FCSTD DOCUMENT  (FreeCAD 0.19R24366 (Git))
Label: collet-mod
License: All rights reserved
LicenseURL: http://en.wikipedia.org/wiki/All_rights_reserved
objects: Part::Feature×53, Part::Cylinder×12, App::Part×10, Part::Chamfer×6, Part::Cut×6, Part::MultiFuse×6
note: 83 computed .brp shape members not serialized (recipe doc carries the construction recipe); baked Part::Feature solids carry a one-line shape summary decoded from their .brp

FEATURE [Part::Feature] Part__Feature  label="shaft^drive_core_sherpa_mini_a3_r9c"
  shape: bbox 5 x 5 x 26.6 mm, 23 faces (baked)
FEATURE [Part::Feature] Part__Feature001  label="0.5mm_shim^drive_core_sherpa_mini_a3_r9c"
  Placement = pos=(0,0,10.3) rot=(0,0,1;0rad)
  shape: bbox 7 x 7 x 0.5 mm, 14 faces (baked)
FEATURE [Part::Feature] Part__Feature002  label="sherpa_mini_gear_50t_sl_7mm^drive_core_sherpa_mini_a3_r9c"
  Placement = pos=(0,0,-10.7) rot=(0,0,1;3.14159rad)
  shape: bbox 34.81 x 38.99 x 7.033 mm, 520 faces (baked)
FEATURE [Part::Feature] Part__Feature003  label="filament_gear^drive_core_sherpa_mini_a3_r9c"
  Placement = pos=(0,0,6.3) rot=(0,0,1;0rad)
  shape: bbox 24.52 x 24.23 x 14.5 mm, 464 faces (baked)
FEATURE [Part::Feature] Part__Feature004  label="MR85-2RS^drive_core_sherpa_mini_a3_r9c"
  Placement = pos=(0,0,12.05) rot=(0,0,1;0rad)
  shape: bbox 8 x 8 x 2.5 mm, 12 faces (baked)
FEATURE [Part::Feature] Part__Feature005  label="MR85-2RS^drive_core_sherpa_mini_a3_r9c001"
  Placement = pos=(0,0,12.05) rot=(0,0,1;0rad)
  shape: bbox 5.6 x 5.6 x 2.5 mm, 14 faces (baked)
FEATURE [Part::Feature] Part__Feature006  label="MR85-2RS^drive_core_sherpa_mini_a3_r9c002"
  Placement = pos=(0,0,12.05) rot=(0,0,1;0rad)
  shape: bbox 7.4 x 7.4 x 2.3 mm, 6 faces (baked)
FEATURE [App::Part] MR85_2RS_drive_core_sherpa_mini_a3_r9c  label="MR85-2RS^drive_core_sherpa_mini_a3_r9c003"
  Group = -> [Part__Feature004,Part__Feature005,Part__Feature006]
  Origin = -> Origin
FEATURE [Part::Feature] Part__Feature007  label="MR85-2RS^drive_core_sherpa_mini_a3_r9c004"
  Placement = pos=(0,0,-12.05) rot=(0,0,1;0rad)
  shape: bbox 8 x 8 x 2.5 mm, 12 faces (baked)
FEATURE [Part::Feature] Part__Feature008  label="MR85-2RS^drive_core_sherpa_mini_a3_r9c005"
  Placement = pos=(0,0,-12.05) rot=(0,0,1;0rad)
  shape: bbox 5.6 x 5.6 x 2.5 mm, 14 faces (baked)
FEATURE [Part::Feature] Part__Feature009  label="MR85-2RS^drive_core_sherpa_mini_a3_r9c006"
  Placement = pos=(0,0,-12.05) rot=(0,0,1;0rad)
  shape: bbox 7.4 x 7.4 x 2.3 mm, 6 faces (baked)
FEATURE [App::Part] MR85_2RS_drive_core_sherpa_mini_a3_r9c001  label="MR85-2RS^drive_core_sherpa_mini_a3_r9c007"
  Group = -> [Part__Feature007,Part__Feature008,Part__Feature009]
  Origin = -> Origin001
FEATURE [Part::Feature] Part__Feature010  label="m3_set_screw^drive_core_sherpa_mini_a3_r9c"
  Placement = pos=(0,2,3.3) rot=(0,0,1;0rad)
  shape: bbox 3.112 x 2.509 x 3.465 mm, 55 faces (baked)
FEATURE [App::Part] drive_core_sherpa_mini_a3_r9c  label="drive_core^sherpa_mini_a3_r9c"
  Group = -> [Part__Feature,Part__Feature001,Part__Feature002,Part__Feature003,MR85_2RS_drive_core_sherpa_mini_a3_r9c,MR85_2RS_drive_core_sherpa_mini_a3_r9c001,Part__Feature010]
  Origin = -> Origin002
  Placement = pos=(0,3.5e-15,6.7) rot=(0,0,1;0rad)
FEATURE [Part::Feature] Part__Feature011  label="housing_core^housing_sherpa_mini_a3_r9c"
  shape: bbox 51.31 x 37.37 x 18.93 mm, 771 faces (baked)
FEATURE [Part::Feature] Part__Feature012  label="housing_front^housing_sherpa_mini_a3_r9c"
  Placement = pos=(3e-15,0,17.5) rot=(0,0,1;0rad)
  shape: bbox 24.8 x 26.5 x 3.9 mm, 96 faces (baked)
FEATURE [Part::Feature] Part__Feature013  label="housing_front_k^housing_sherpa_mini_a3_r9c"
  Placement = pos=(-2e-16,0,17.5) rot=(0,0,1;0rad)
  shape: bbox 24.8 x 34.5 x 3.9 mm, 105 faces (baked)
FEATURE [Part::Feature] Part__Feature014  label="housing_rear_nema14^housing_sherpa_mini_a3_r9c"
  Placement = pos=(2e-15,-4e-15,-7) rot=(0,0,1;0rad)
  shape: bbox 51.24 x 47.65 x 9.996 mm, 527 faces (baked)
FEATURE [Part::Feature] Part__Feature015  label="idler_arm_short^housing_sherpa_mini_a3_r9c"
  Placement = pos=(-3e-15,0,4.25) rot=(0,0,1;0rad)
  shape: bbox 10.71 x 27.26 x 21.6 mm, 303 faces (baked)
FEATURE [Part::Feature] Part__Feature016  label="idler_arm_long^housing_sherpa_mini_a3_r9c"
  Placement = pos=(0,0,4.25) rot=(0,0,1;0rad)
  shape: bbox 10.86 x 38.76 x 21.68 mm, 332 faces (baked)
FEATURE [App::Part] housing_sherpa_mini_a3_r9c  label="housing^sherpa_mini_a3_r9c"
  Group = -> [Part__Feature011,Part__Feature012,Part__Feature013,Part__Feature014,Part__Feature015,Part__Feature016]
  Origin = -> Origin003
FEATURE [Part::Feature] Part__Feature017  label="idler_pin^sherpa_mini_a3_r9c"
  Placement = pos=(13.1,-9.8,0.25) rot=(0,0,1;0rad)
  shape: bbox 3 x 3 x 20 mm, 8 faces (baked)
FEATURE [Part::Feature] Part__Feature018  label="idler_gear^idler_gear_assy_sherpa_mini_a3_r9c"
  Placement = pos=(0,0,2.4) rot=(0,0,1;0.1848rad)
  shape: bbox 24.52 x 24.41 x 14.5 mm, 457 faces (baked)
FEATURE [Part::Feature] Part__Feature019  label="shaft^idler_gear_assy_sherpa_mini_a3_r9c"
  shape: bbox 3 x 3 x 20 mm, 8 faces (baked)
FEATURE [Part::Feature] Part__Feature020  label="needle_bearing^idler_gear_assy_sherpa_mini_a3_r9c"
  Placement = pos=(0,0,-4.35) rot=(0,0,1;0.1848rad)
  shape: bbox 1 x 1 x 4.25 mm, 8 faces (baked)
FEATURE [Part::Feature] Part__Feature021  label="needle_bearing^idler_gear_assy_sherpa_mini_a3_r9c001"
  Placement = pos=(0,0,-4.35) rot=(0,0,1;0.1848rad)
  shape: bbox 4.8 x 4.8 x 6.5 mm, 82 faces (baked)
FEATURE [Part::Feature] Part__Feature022  label="needle_bearing^idler_gear_assy_sherpa_mini_a3_r9c002"
  Placement = pos=(0,0,-4.35) rot=(0,0,1;0.1848rad)
  shape: bbox 1 x 1 x 4.25 mm, 8 faces (baked)
FEATURE [Part::Feature] Part__Feature023  label="needle_bearing^idler_gear_assy_sherpa_mini_a3_r9c003"
  Placement = pos=(0,0,-4.35) rot=(0,0,1;0.1848rad)
  shape: bbox 1 x 1 x 4.25 mm, 8 faces (baked)
FEATURE [Part::Feature] Part__Feature024  label="needle_bearing^idler_gear_assy_sherpa_mini_a3_r9c004"
  Placement = pos=(0,0,-4.35) rot=(0,0,1;0.1848rad)
  shape: bbox 1 x 1 x 4.25 mm, 8 faces (baked)
FEATURE [Part::Feature] Part__Feature025  label="needle_bearing^idler_gear_assy_sherpa_mini_a3_r9c005"
  Placement = pos=(0,0,-4.35) rot=(0,0,1;0.1848rad)
  shape: bbox 1 x 1 x 4.25 mm, 8 faces (baked)
FEATURE [Part::Feature] Part__Feature026  label="needle_bearing^idler_gear_assy_sherpa_mini_a3_r9c006"
  Placement = pos=(0,0,-4.35) rot=(0,0,1;0.1848rad)
  shape: bbox 1 x 1 x 4.25 mm, 8 faces (baked)
FEATURE [Part::Feature] Part__Feature027  label="needle_bearing^idler_gear_assy_sherpa_mini_a3_r9c007"
  Placement = pos=(0,0,-4.35) rot=(0,0,1;0.1848rad)
  shape: bbox 1 x 1 x 4.25 mm, 8 faces (baked)
FEATURE [App::Part] needle_bearing_idler_gear_assy_sherpa_mini_a3_r9c  label="needle_bearing^idler_gear_assy_sherpa_mini_a3_r9c008"
  Group = -> [Part__Feature020,Part__Feature021,Part__Feature022,Part__Feature023,Part__Feature024,Part__Feature025,Part__Feature026,Part__Feature027]
  Origin = -> Origin004
FEATURE [Part::Feature] Part__Feature028  label="needle_bearing^idler_gear_assy_sherpa_mini_a3_r9c009"
  Placement = pos=(0,0,3.15) rot=(0,0,1;0.1848rad)
  shape: bbox 1 x 1 x 4.25 mm, 8 faces (baked)
FEATURE [Part::Feature] Part__Feature029  label="needle_bearing^idler_gear_assy_sherpa_mini_a3_r9c010"
  Placement = pos=(0,0,3.15) rot=(0,0,1;0.1848rad)
  shape: bbox 4.8 x 4.8 x 6.5 mm, 82 faces (baked)
FEATURE [Part::Feature] Part__Feature030  label="needle_bearing^idler_gear_assy_sherpa_mini_a3_r9c011"
  Placement = pos=(0,0,3.15) rot=(0,0,1;0.1848rad)
  shape: bbox 1 x 1 x 4.25 mm, 8 faces (baked)
FEATURE [Part::Feature] Part__Feature031  label="needle_bearing^idler_gear_assy_sherpa_mini_a3_r9c012"
  Placement = pos=(0,0,3.15) rot=(0,0,1;0.1848rad)
  shape: bbox 1 x 1 x 4.25 mm, 8 faces (baked)
FEATURE [Part::Feature] Part__Feature032  label="needle_bearing^idler_gear_assy_sherpa_mini_a3_r9c013"
  Placement = pos=(0,0,3.15) rot=(0,0,1;0.1848rad)
  shape: bbox 1 x 1 x 4.25 mm, 8 faces (baked)
FEATURE [Part::Feature] Part__Feature033  label="needle_bearing^idler_gear_assy_sherpa_mini_a3_r9c014"
  Placement = pos=(0,0,3.15) rot=(0,0,1;0.1848rad)
  shape: bbox 1 x 1 x 4.25 mm, 8 faces (baked)
FEATURE [Part::Feature] Part__Feature034  label="needle_bearing^idler_gear_assy_sherpa_mini_a3_r9c015"
  Placement = pos=(0,0,3.15) rot=(0,0,1;0.1848rad)
  shape: bbox 1 x 1 x 4.25 mm, 8 faces (baked)
FEATURE [Part::Feature] Part__Feature035  label="needle_bearing^idler_gear_assy_sherpa_mini_a3_r9c016"
  Placement = pos=(0,0,3.15) rot=(0,0,1;0.1848rad)
  shape: bbox 1 x 1 x 4.25 mm, 8 faces (baked)
FEATURE [App::Part] needle_bearing_idler_gear_assy_sherpa_mini_a3_r9c001  label="needle_bearing^idler_gear_assy_sherpa_mini_a3_r9c017"
  Group = -> [Part__Feature028,Part__Feature029,Part__Feature030,Part__Feature031,Part__Feature032,Part__Feature033,Part__Feature034,Part__Feature035]
  Origin = -> Origin005
FEATURE [App::Part] idler_gear_assy_sherpa_mini_a3_r9c  label="idler_gear_assy^sherpa_mini_a3_r9c"
  Group = -> [Part__Feature018,Part__Feature019,needle_bearing_idler_gear_assy_sherpa_mini_a3_r9c,needle_bearing_idler_gear_assy_sherpa_mini_a3_r9c001]
  Origin = -> Origin006
  Placement = pos=(8.6,0,10.6) rot=(0,0,1;0rad)
FEATURE [Part::Feature] Part__Feature036  label="NEMA14_10t^sherpa_mini_a3_r9c"
  Placement = pos=(4.3,-11.3907,-1) rot=(0,0,1;0rad)
  shape: bbox 50.9 x 36.5 x 23.5 mm, 227 faces (baked)
FEATURE [Part::Feature] Part__Feature037  label="socket button head screw_iso_ISO 7380 - M3 x 12 - 12N"
  Placement = pos=(26.2203,14.1093,4.65) rot=(0,1,0;1.5708rad)
  shape: bbox 5.7 x 5.7 x 13.97 mm, 27 faces (baked)
FEATURE [Part::Feature] Part__Feature038  label="socket button head screw_iso_ISO 7380 - M3 x 12 - 12N001"
  Placement = pos=(-17.6203,14.1093,4.65) rot=(0,1,0;1.5708rad)
  shape: bbox 5.7 x 5.7 x 13.97 mm, 27 faces (baked)
FEATURE [Part::Feature] Part__Feature039  label="socket button head screw_iso_ISO 7380 - M3 x 16 - 16N"
  Placement = pos=(22.65,-9.8,11.65) rot=(0,1,0;1.5708rad)
  shape: bbox 5.7 x 5.7 x 17.97 mm, 27 faces (baked)
FEATURE [Part::Feature] Part__Feature040  label="socket button head screw_iso_ISO 7380 - M3 x 16 - 16N001"
  Placement = pos=(-14.05,-9.8,11.65) rot=(0,1,0;1.5708rad)
  shape: bbox 5.7 x 5.7 x 17.97 mm, 27 faces (baked)
FEATURE [Part::Feature] Part__Feature041  label="socket button head screw_iso_ISO 7380 - M3 x 8 - 8N"
  Placement = pos=(0,9,21.9) rot=(0.707107,0,-0.707107;3.14159rad)
  shape: bbox 5.7 x 5.7 x 9.968 mm, 27 faces (baked)
FEATURE [Part::Feature] Part__Feature042  label="socket button head screw_iso_ISO 7380 - M3 x 8 - 8N001"
  Placement = pos=(5e-15,-9,21.9) rot=(0.707107,0,-0.707107;3.14159rad)
  shape: bbox 5.7 x 5.7 x 9.968 mm, 27 faces (baked)
FEATURE [Part::Feature] Part__Feature043  label="insert_m3x5x4"
  Placement = pos=(11.2,9.75,10.25) rot=(-0.485903,0.726496,-0.485903;1.88502rad)
  shape: bbox 5.246 x 5.066 x 5.066 mm, 280 faces (baked)
FEATURE [Part::Feature] Part__Feature044  label="insert_m3x5x005"
  Placement = pos=(1e-15,9,17.5) rot=(0,0,-1;0.785905rad)
  shape: bbox 5.062 x 5.062 x 5.246 mm, 280 faces (baked)
FEATURE [Part::Feature] Part__Feature045  label="insert_m3x5x006"
  Placement = pos=(2e-15,-9,17.5) rot=(0,0,-1;0.785905rad)
  shape: bbox 5.062 x 5.062 x 5.246 mm, 280 faces (baked)
FEATURE [Part::Feature] Part__Feature046  label="insert_m3x5x007"
  Placement = pos=(22.65,-9.8,-7) rot=(0,1,0;3.14159rad)
  shape: bbox 5.062 x 5.062 x 5.246 mm, 280 faces (baked)
FEATURE [Part::Feature] Part__Feature047  label="insert_m3x5x008"
  Placement = pos=(-14.05,-9.8,-7) rot=(0,1,0;3.14159rad)
  shape: bbox 5.062 x 5.062 x 5.246 mm, 280 faces (baked)
FEATURE [Part::Feature] Part__Feature048  label="thumbscrew^thumbscrew"
  shape: bbox 5 x 5 x 23.01 mm, 97 faces (baked)
FEATURE [Part::Feature] Part__Feature049  label="thumbscrew^thumbscrew001"
  shape: bbox 12.15 x 12.15 x 3.677 mm, 2617 faces (baked)
FEATURE [App::Part] thumbscrew_thumbscrew  label="thumbscrew^thumbscrew002"
  Group = -> [Part__Feature048,Part__Feature049]
  Origin = -> Origin007
FEATURE [Part::Feature] Part__Feature050  label="spring^thumbscrew"
  Placement = pos=(2e-15,0,16) rot=(0,0,1;0rad)
  shape: bbox 7.392 x 7.388 x 14 mm, 6 faces (baked)
FEATURE [App::Part] thumbscrew
  Group = -> [thumbscrew_thumbscrew,Part__Feature050]
  Origin = -> Origin008
  Placement = pos=(32.8,9.75,10.25) rot=(0,-1,0;1.5708rad)
FEATURE [App::Part] sherpa_mini_a3_r9c_nema_14
  Group = -> [drive_core_sherpa_mini_a3_r9c,housing_sherpa_mini_a3_r9c,Part__Feature017,idler_gear_assy_sherpa_mini_a3_r9c,Part__Feature036,Part__Feature037,Part__Feature038,Part__Feature039,Part__Feature040,Part__Feature041,Part__Feature042,Part__Feature043,Part__Feature044,Part__Feature045,Part__Feature046,Part__Feature047,thumbscrew]
  Origin = -> Origin009
FEATURE [Part::Cylinder] Cylinder
  Angle = 360
  AttacherType = Attacher::AttachEngine3D
  Height = 4
  Placement = pos=(4.3,11.81,6) rot=(-1,0,0;1.5708rad)
  Radius = 3.5
FEATURE [Part::Cylinder] Cylinder001
  Angle = 360
  AttacherType = Attacher::AttachEngine3D
  Height = 7
  Placement = pos=(4.3,10.81,6) rot=(-1,0,0;1.5708rad)
  Radius = 5
FEATURE [Part::Chamfer] Chamfer
  Base = -> Cylinder001
  Edges = 1 edges r=1: [Edge3]
FEATURE [Part::Chamfer] Chamfer001
  Base = -> Chamfer
  Edges = 1 edges r=0.4: [Edge3]
FEATURE [Part::Cylinder] Cylinder003
  Angle = 360
  AttacherType = Attacher::AttachEngine3D
  Height = 5
  Placement = pos=(4.3,12.81,6) rot=(-1,0,0;1.5708rad)
  Radius = 2.5
FEATURE [Part::Cylinder] Cylinder004
  Angle = 360
  AttacherType = Attacher::AttachEngine3D
  Height = 12.5
  Placement = pos=(4.3,5.31,6) rot=(-1,0,0;1.5708rad)
  Radius = 3
FEATURE [Part::Cylinder] Cylinder005
  Angle = 360
  AttacherType = Attacher::AttachEngine3D
  Height = 12.5
  Placement = pos=(4.3,19.81,6) rot=(-1,0,0;1.5708rad)
  Radius = 2.2
FEATURE [Part::Cylinder] Cylinder006
  Angle = 360
  AttacherType = Attacher::AttachEngine3D
  Height = 12.5
  Placement = pos=(4.3,5.31,6) rot=(-1,0,0;1.5708rad)
  Radius = 1
FEATURE [Part::Cut] Cut
  Base = -> Cylinder004
  Tool = -> Cylinder006
FEATURE [Part::MultiFuse] Fusion
  Shapes = -> [Part__Feature011,Cut]
FEATURE [Part::Chamfer] Chamfer002
  Base = -> Cylinder005
  Edges = 1 edges r=1: [Edge3]
  Placement = pos=(0,-14.5,0) rot=(0,0,1;0rad)
FEATURE [Part::Cut] Cut001
  Base = -> Fusion
  Tool = -> Chamfer002
FEATURE [Part::Cylinder] Cylinder007
  Angle = 360
  AttacherType = Attacher::AttachEngine3D
  Height = 5
  Placement = pos=(4.3,9.31,6) rot=(-1,0,0;1.5708rad)
  Radius = 2.2
FEATURE [Part::MultiFuse] Fusion002
  Shapes = -> [Cylinder007,Cylinder003]
FEATURE [Part::Cylinder] Cylinder008
  Angle = 360
  AttacherType = Attacher::AttachEngine3D
  Height = 4
  Placement = pos=(13.1,-9.8,0) rot=(0,0,1;0rad)
  Radius = 1.5
FEATURE [Part::Cylinder] Cylinder009
  Angle = 360
  AttacherType = Attacher::AttachEngine3D
  Height = 4
  Placement = pos=(13.1,-9.8,0) rot=(0,0,1;0rad)
  Radius = 3
FEATURE [Part::Cylinder] Cylinder010
  Angle = 360
  AttacherType = Attacher::AttachEngine3D
  Height = 10
  Placement = pos=(5,9.75,10.2) rot=(0,1,0;1.5708rad)
  Radius = 2.5
FEATURE [Part::Cut] Cut002
  Base = -> Chamfer001
  Tool = -> Cylinder010
FEATURE [Part::MultiFuse] Fusion003
  Shapes = -> [Cut002,Cut001]
FEATURE [Part::MultiFuse] Fusion004
  Shapes = -> [Cylinder,Fusion002]
FEATURE [Part::Cut] Cut003
  Base = -> Fusion003
  Tool = -> Fusion004
FEATURE [Part::MultiFuse] Fusion005
  Shapes = -> [Cylinder009,Cut003]
FEATURE [Part::Cut] Cut004  label="base"
  Base = -> Fusion005
  Tool = -> Cylinder008
FEATURE [Part::Feature] Cut004001  label="base001"
  shape: bbox 51.31 x 37.37 x 18.93 mm, 694 faces (baked)
FEATURE [Part::Chamfer] Chamfer003  label="e3d-mod"
  Base = -> Cut004001
  Edges = 2 edges r=0.4: [Edge1546,Edge1552]
FEATURE [Part::Cylinder] Cylinder011
  Angle = 360
  AttacherType = Attacher::AttachEngine3D
  Height = 5
  Placement = pos=(4.3,10.81,6) rot=(-1,0,0;1.5708rad)
  Radius = 4.25
FEATURE [Part::Feature] Chamfer003001
  shape: bbox 51.31 x 37.37 x 18.93 mm, 696 faces (baked)
FEATURE [Part::Cylinder] Cylinder012
  Angle = 360
  AttacherType = Attacher::AttachEngine3D
  Height = 4
  Placement = pos=(4.3,14.81,6) rot=(-1,0,0;1.5708rad)
  Radius = 3.2
FEATURE [Part::Chamfer] Chamfer003002
  Base = -> Cylinder011
  Edges = 1 edges r=1.5: [Edge3]
FEATURE [Part::MultiFuse] Fusion006
  Shapes = -> [Chamfer003002,Cylinder012]
FEATURE [Part::Cut] Cut004002
  Base = -> Chamfer003001
  Tool = -> Fusion006
FEATURE [Part::Chamfer] Chamfer003003  label="triangle-lab-mod"
  Base = -> Cut004002
  Edges = 2 edges r=0.4: [Edge2,Edge11]
